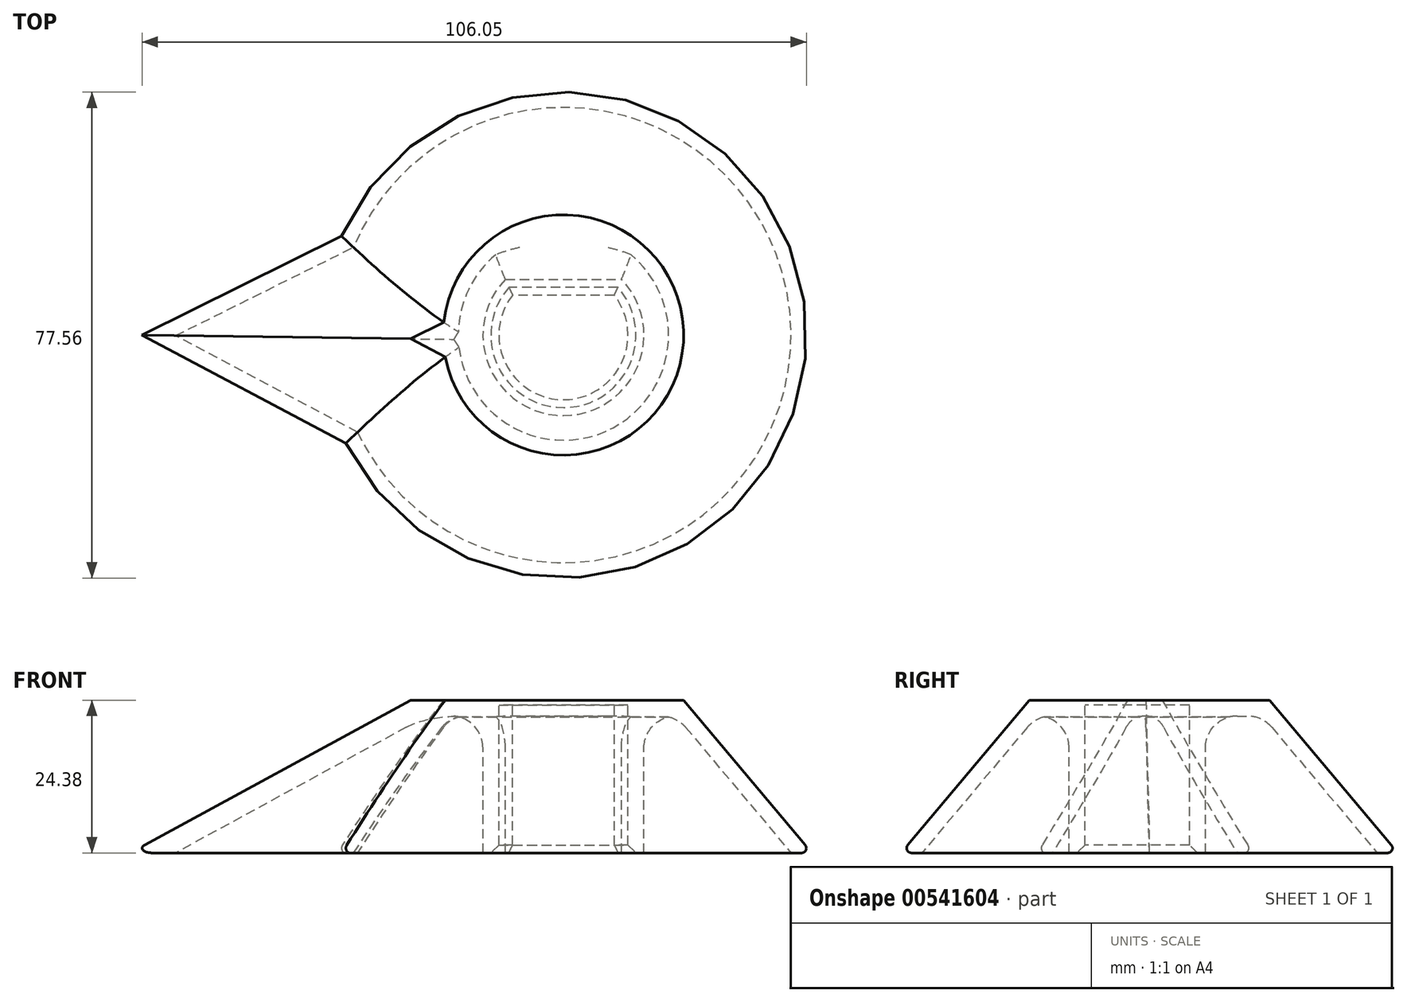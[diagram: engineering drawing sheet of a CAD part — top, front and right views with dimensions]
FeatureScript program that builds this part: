
annotation { "Feature Type Name" : "Feature", "Feature Type Description" : "" }
export const myFeature = defineFeature(function(context is Context, id is Id, definition is map)
    precondition{}
    {
        {
            var Q0;
            Q0=qCreatedBy(makeId("Top.planeOp"),FACE);
            var sketch = newSketch(context, id + "F0", { "sketchPlane" : qUnion([Q0])});
            skArc(sketch, "E0", {"start": v(-35.37, -17.92) * mm, "mid": v(39.64, 0.82) * mm, "end": v(-36.08, 16.44) * mm});
            skLineSegment(sketch, "E1", {"start": v(-36.08, 16.44) * mm, "end": v(-69.18, 0) * mm});
            skLineSegment(sketch, "E2", {"start": v(-69.18, 0) * mm, "end": v(-35.37, -17.92) * mm});
            skSolve(sketch);
        }
        {
            var Q0;
            Q0=qSketchRegion(id+"F0",true);
            extrude(context, id + "F1", {"entities" : qUnion([Q0]), "depth" : 24.38 * mm, "offsetDistance" : 25.4 * mm, "hasDraft" : true, "draftAngle" : 40 * degree, "draftPullDirection" : true});
        }
        {
            var Q0;
            Q0=makeQuery(id+"F1.opExtrude","CAP_FACE",FACE,{"disambiguationData":[OSD([sQuery(id+"F0.wireOp",EDGE,"E0"),sQuery(id+"F0.wireOp",EDGE,"E1"),sQuery(id+"F0.wireOp",EDGE,"E2")])],"isStart":false});
            var sketch = newSketch(context, id + "F2", { "sketchPlane" : qUnion([Q0])});
            skArc(sketch, "E3", {"start": v(-8.1, 6.37) * mm, "mid": v(0, -10.31) * mm, "end": v(8.1, 6.37) * mm});
            skLineSegment(sketch, "E4", {"start": v(-8.1, 6.37) * mm, "end": v(8.1, 6.37) * mm});
            skSolve(sketch);
        }
        {
            var Q0;
            Q0=qSketchRegion(id+"F2",true);
            extrude(context, id + "F3", {"entities" : qUnion([Q0]), "operationType" : NewBodyOperationType.REMOVE, "oppositeDirection" : true, "depth" : 35.3 * mm, "offsetDistance" : 25.4 * mm});
        }
        {
            var Q0;
            Q0=makeQuery(id+"F1.opExtrude","CAP_FACE",FACE,{"disambiguationData":[OSD([sQuery(id+"F0.wireOp",EDGE,"E0"),sQuery(id+"F0.wireOp",EDGE,"E1"),sQuery(id+"F0.wireOp",EDGE,"E2")])],"isStart":true});
            shell(context, id + "F4", {"entities" : qUnion([Q0]), "thickness" : 2.54 * mm});
        }
        {
            var Q0;
            {var subQ0=sQuery(id+"F0.wireOp",EDGE,"E2");var subQ1=sQuery(id+"F0.wireOp",EDGE,"E1");var subQ2=sQuery(id+"F0.wireOp",EDGE,"E0");Q0=makeQuery(id+"F4.opShell","OFFSET_FACE",FACE,{"disambiguationData":[OSD([subQ2,subQ1,subQ0]),TDD([makeQuery(id+"F1.opExtrude","CAP_FACE",FACE,{"disambiguationData":[OSD([subQ2,subQ1,subQ0])],"isStart":false})])]});}
            fillet(context, id + "F5", {"entities" : qUnion([Q0]), "radius" : 5.08 * mm, "tangentPropagation" : true, "allowEdgeOverflow" : false});
        }
        {
            var Q0;
            Q0=makeQuery(id+"F1.opExtrude","CAP_EDGE",EDGE,{"disambiguationData":[OSD([sQuery(id+"F0.wireOp",EDGE,"E0")])],"isStart":true});
            var Q1;
            Q1=makeQuery(id+"F1.opExtrude","CAP_EDGE",EDGE,{"disambiguationData":[OSD([sQuery(id+"F0.wireOp",EDGE,"E2")])],"isStart":true});
            var Q2;
            Q2=makeQuery(id+"F1.opExtrude","CAP_EDGE",EDGE,{"disambiguationData":[OSD([sQuery(id+"F0.wireOp",EDGE,"E1")])],"isStart":true});
            fillet(context, id + "F6", {"entities" : qUnion([Q0, Q1, Q2]), "radius" : 0.76 * mm, "tangentPropagation" : true, "allowEdgeOverflow" : false});
        }
        {
            var Q0;
            Q0=makeQuery(id+"F3.boolean.opBoolean","INTERSECT",EDGE,{"derivedFrom":[makeQuery(id+"F1.opExtrude","CAP_FACE",FACE,{"disambiguationData":[OSD([sQuery(id+"F0.wireOp",EDGE,"E0"),sQuery(id+"F0.wireOp",EDGE,"E1"),sQuery(id+"F0.wireOp",EDGE,"E2")])],"isStart":true}),makeQuery(id+"F3.opExtrude","SWEPT_FACE",FACE,{"disambiguationData":[OSD([sQuery(id+"F2.wireOp",EDGE,"E4")])]})]});
            var Q1;
            Q1=makeQuery(id+"F3.boolean.opBoolean","INTERSECT",EDGE,{"derivedFrom":[makeQuery(id+"F1.opExtrude","CAP_FACE",FACE,{"disambiguationData":[OSD([sQuery(id+"F0.wireOp",EDGE,"E0"),sQuery(id+"F0.wireOp",EDGE,"E1"),sQuery(id+"F0.wireOp",EDGE,"E2")])],"isStart":true}),makeQuery(id+"F3.opExtrude","SWEPT_FACE",FACE,{"disambiguationData":[OSD([sQuery(id+"F2.wireOp",EDGE,"E3")])]})]});
            chamfer(context, id + "F7", {"entities" : qUnion([Q0, Q1]), "width" : 1.27 * mm, "tangentPropagation" : true});
        }
        {
            var Q0;
            Q0=makeQuery(id+"F1.opExtrude","CAP_FACE",FACE,{"disambiguationData":[OSD([sQuery(id+"F0.wireOp",EDGE,"E0"),sQuery(id+"F0.wireOp",EDGE,"E1"),sQuery(id+"F0.wireOp",EDGE,"E2")])],"isStart":false});
            var sketch = newSketch(context, id + "F8", { "sketchPlane" : qUnion([Q0])});
            skCircle(sketch, "E5", {"center": v(0, 0) * mm, "radius": 14.86 * mm});
            skSolve(sketch);
        }
        {
            var Q0;
            Q0 = qSketchRegion(id + "F8", true);
            extrude(context, id + "F9", {"entities" : qUnion([Q0]), "operationType" : NewBodyOperationType.ADD, "oppositeDirection" : true, "depth" : 0.76 * mm, "offsetDistance" : 25.4 * mm});
        }
    });
